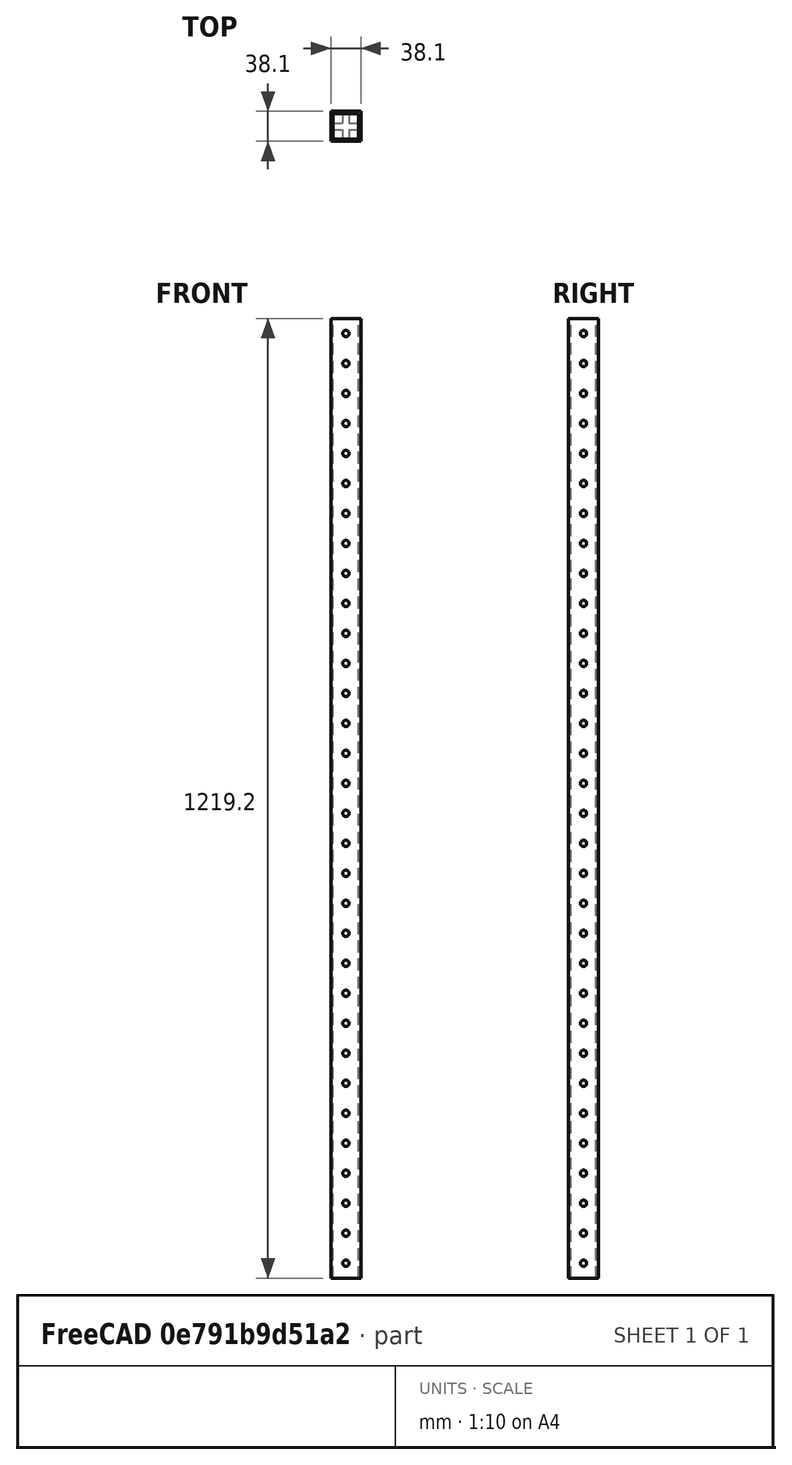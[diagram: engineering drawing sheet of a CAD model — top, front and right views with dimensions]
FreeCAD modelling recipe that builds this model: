
FCSTD DOCUMENT  (FreeCAD 0.15R4671 (Git))
Label: base-model
License: All rights reserved
LicenseURL: http://en.wikipedia.org/wiki/All_rights_reserved
objects: Part::Box×2, Part::Cylinder×2, Part::FeaturePython×2
note: 6 computed .brp shape members not serialized (recipe doc carries the construction recipe); baked Part::Feature solids carry a one-line shape summary decoded from their .brp

FEATURE [Part::Box] Box  label="Beam"
  Height = 1219.2
  Length = 38.1
  Width = 38.1
FEATURE [Part::Cylinder] Cylinder
  Angle = 360
  Height = 38.1
  Placement = pos=(0,19.05,19.05) rot=(0,1,0;1.5708rad)
  Radius = 4
FEATURE [Part::Cylinder] Cylinder001
  Angle = 360
  Height = 38.1
  Placement = pos=(19.05,38.1,19.05) rot=(1,0,0;1.5708rad)
  Radius = 4
FEATURE [Part::FeaturePython] Array  label="Holes1"  # Draft array (typed FeaturePython)
  Angle = 360
  ArrayType = 0
  Axis = (0,0,1)
  Base = -> Cylinder001
  Center = (0,0,0)
  Fuse = false
  IntervalAxis = (0,0,0)
  IntervalX = (1,0,0)
  IntervalY = (0,1,0)
  IntervalZ = (0,0,38.1)
  NumberPolar = 1
  NumberX = 1
  NumberY = 1
  NumberZ = 32
FEATURE [Part::FeaturePython] Array001  label="Holes2"  # Draft array (typed FeaturePython)
  Angle = 360
  ArrayType = 0
  Axis = (0,0,1)
  Base = -> Cylinder
  Center = (0,0,0)
  Fuse = false
  IntervalAxis = (0,0,0)
  IntervalX = (1,0,0)
  IntervalY = (0,1,0)
  IntervalZ = (0,0,38.1)
  NumberPolar = 1
  NumberX = 1
  NumberY = 1
  NumberZ = 32
FEATURE [Part::Box] Box001  label="Cutout"
  Height = 1219.2
  Length = 32.1
  Placement = pos=(3,3,0) rot=(0,0,1;0rad)
  Width = 32.1
